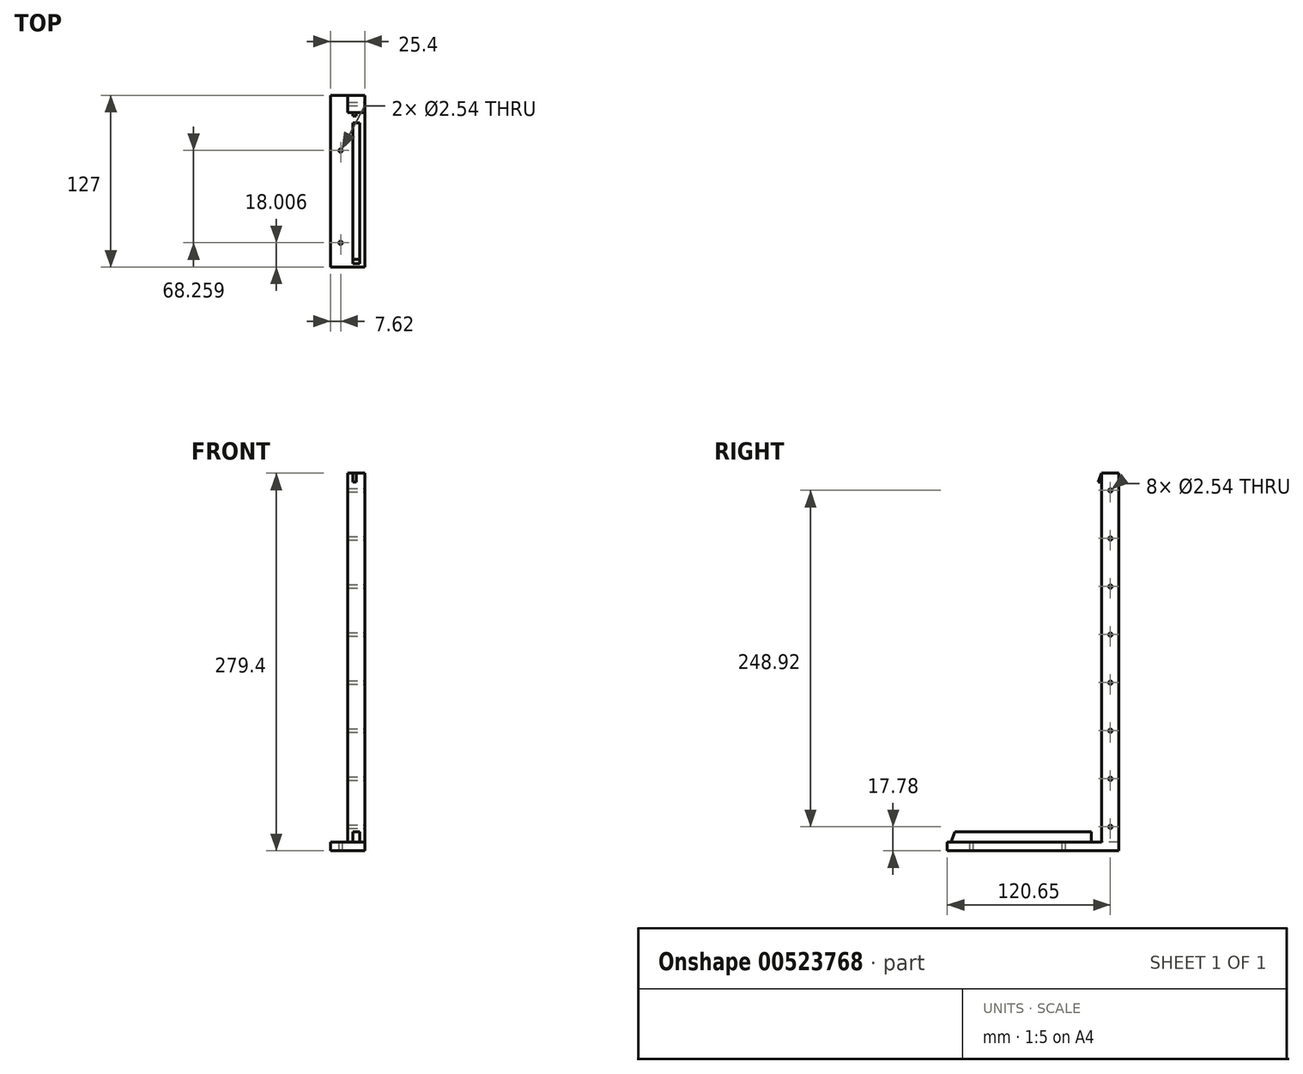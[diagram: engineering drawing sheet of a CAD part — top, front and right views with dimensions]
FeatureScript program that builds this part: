
annotation { "Feature Type Name" : "Feature", "Feature Type Description" : "" }
export const myFeature = defineFeature(function(context is Context, id is Id, definition is map)
    precondition{}
    {
        {
            var Q0;
            Q0=qCreatedBy(makeId("Top.planeOp"),FACE);
            var sketch = newSketch(context, id + "F0", { "sketchPlane" : qUnion([Q0])});
            skLineSegment(sketch, "E0.bottom", {"start": v(0, 0) * mm, "end": v(-25.4, 0) * mm});
            skLineSegment(sketch, "E0.top", {"start": v(0, 127) * mm, "end": v(-25.4, 127) * mm});
            skLineSegment(sketch, "E0.left", {"start": v(0, 0) * mm, "end": v(0, 127) * mm});
            skLineSegment(sketch, "E0.right", {"start": v(-25.4, 0) * mm, "end": v(-25.4, 127) * mm});
            skSolve(sketch);
        }
        {
            var Q0;
            Q0=makeQuery(id+"F0.imprint","IMPRINT",FACE,{"disambiguationData":[TD([[makeQuery(id+"F0.imprint","IMPRINT",EDGE,{"derivedFrom":sQuery(id+"F0.wireOp",EDGE,"E0.bottom")}),-1.0]])]});
            extrude(context, id + "F1", {"entities" : qUnion([Q0]), "depth" : 6.35 * mm, "offsetDistance" : 25.4 * mm});
        }
        {
            var Q0;
            Q0=makeQuery(id+"F1.opExtrude","CAP_FACE",FACE,{"disambiguationData":[OSD([sQuery(id+"F0.wireOp",EDGE,"E0.bottom"),sQuery(id+"F0.wireOp",EDGE,"E0.top"),sQuery(id+"F0.wireOp",EDGE,"E0.left"),sQuery(id+"F0.wireOp",EDGE,"E0.right")])],"isStart":false});
            var sketch = newSketch(context, id + "F2", { "sketchPlane" : qUnion([Q0])});
            skLineSegment(sketch, "E1.bottom", {"start": v(-25.4, 127) * mm, "end": v(-12.7, 127) * mm});
            skLineSegment(sketch, "E1.top", {"start": v(-25.4, 114.3) * mm, "end": v(-12.7, 114.3) * mm});
            skLineSegment(sketch, "E1.left", {"start": v(-25.4, 127) * mm, "end": v(-25.4, 114.3) * mm});
            skLineSegment(sketch, "E1.right", {"start": v(-12.7, 127) * mm, "end": v(-12.7, 114.3) * mm});
            skSolve(sketch);
        }
        {
            var Q0;
            Q0=makeQuery(id+"F2.imprint","IMPRINT",FACE,{"disambiguationData":[TD([[makeQuery(id+"F2.imprint","IMPRINT",EDGE,{"derivedFrom":sQuery(id+"F2.wireOp",EDGE,"E1.bottom")}),1.0]])]});
            extrude(context, id + "F3", {"entities" : qUnion([Q0]), "operationType" : NewBodyOperationType.ADD, "depth" : 273.05 * mm, "offsetDistance" : 25.4 * mm});
        }
        {
            var Q0;
            Q0=makeQuery(id+"F3.opExtrude","SWEPT_FACE",FACE,{"disambiguationData":[OSD([sQuery(id+"F2.wireOp",EDGE,"E1.top")])]});
            var sketch = newSketch(context, id + "F4", { "sketchPlane" : qUnion([Q0])});
            skLineSegment(sketch, "E2", {"start": v(-19.05, 279.4) * mm, "end": v(-19.05, 272.87) * mm});
            skLineSegment(sketch, "E3", {"start": v(-19.05, 272.87) * mm, "end": v(-21.59, 272.87) * mm});
            skLineSegment(sketch, "E4.top", {"start": v(-19.05, 279.4) * mm, "end": v(-21.59, 279.4) * mm});
            skLineSegment(sketch, "E4.left", {"start": v(-19.05, 272.87) * mm, "end": v(-19.05, 279.4) * mm});
            skLineSegment(sketch, "E4.right", {"start": v(-21.59, 272.87) * mm, "end": v(-21.59, 279.4) * mm});
            skSolve(sketch);
        }
        {
            var Q0;
            Q0=makeQuery(id+"F4.imprint","IMPRINT",FACE,{"disambiguationData":[TD([[makeQuery(id+"F4.imprint","IMPRINT",EDGE,{"derivedFrom":sQuery(id+"F4.wireOp",EDGE,"E3")}),-1.0]])]});
            extrude(context, id + "F5", {"entities" : qUnion([Q0]), "operationType" : NewBodyOperationType.ADD, "depth" : 25.4 * mm, "offsetDistance" : 25.4 * mm});
        }
        {
            var Q0;
            Q0=makeQuery(id+"F5.opExtrude","SWEPT_FACE",FACE,{"disambiguationData":[OSD([sQuery(id+"F4.wireOp",EDGE,"E4.right")])]});
            var sketch = newSketch(context, id + "F6", { "sketchPlane" : qUnion([Q0])});
            skLineSegment(sketch, "E5", {"start": v(-114.3, 279.4) * mm, "end": v(0, 0) * mm});
            skLineSegment(sketch, "E6", {"start": v(0, 0) * mm, "end": v(-114.3, 0) * mm});
            skLineSegment(sketch, "E7", {"start": v(-114.3, 0) * mm, "end": v(-114.3, 279.4) * mm});
            skLineSegment(sketch, "E8", {"start": v(-114.3, 0) * mm, "end": v(-96.32, 0) * mm});
            skLineSegment(sketch, "E9", {"start": v(-114.3, 0) * mm, "end": v(-114.3, 6.35) * mm});
            skLineSegment(sketch, "E10", {"start": v(-114.3, 6.35) * mm, "end": v(-106.68, 6.35) * mm});
            skLineSegment(sketch, "E11", {"start": v(-106.68, 6.35) * mm, "end": v(-106.68, 13.97) * mm});
            skLineSegment(sketch, "E12", {"start": v(-106.68, 13.97) * mm, "end": v(-5.71, 13.97) * mm});
            skLineSegment(sketch, "E13", {"start": v(-5.71, 13.97) * mm, "end": v(-13.34, 13.97) * mm});
            skLineSegment(sketch, "E14", {"start": v(-114.3, 279.4) * mm, "end": v(-114.3, 263.18) * mm});
            skLineSegment(sketch, "E15", {"start": v(-106.68, 13.97) * mm, "end": v(-106.68, 217.25) * mm});
            skLineSegment(sketch, "E16", {"start": v(-106.68, 217.25) * mm, "end": v(-106.68, 237.58) * mm});
            skLineSegment(sketch, "E17", {"start": v(-106.68, 237.58) * mm, "end": v(-13.33, 13.97) * mm});
            skSolve(sketch);
        }
        {
            var Q0;
            {var subQ5=sQuery(id+"F6.wireOp",EDGE,"E7");Q0=makeQuery(id+"F6.imprint","IMPRINT",FACE,{"disambiguationData":[TD([[makeQuery(id+"F6.imprint","IMPRINT",EDGE,{"derivedFrom":subQ5}),-1.0]])]});}
            var Q1;
            {var subQ0=sQuery(id+"F6.wireOp",EDGE,"E6");Q1=makeQuery(id+"F6.imprint","IMPRINT",FACE,{"disambiguationData":[TD([[makeQuery(id+"F6.imprint","IMPRINT",EDGE,{"derivedFrom":subQ0}),-1.0]])]});}
            extrude(context, id + "F7", {"entities" : qUnion([Q0, Q1]), "operationType" : NewBodyOperationType.ADD, "oppositeDirection" : true, "depth" : 5.08 * mm, "offsetDistance" : 25.4 * mm});
        }
        {
            var Q0;
            Q0=makeQuery(id+"F5.opExtrude","CAP_FACE",FACE,{"disambiguationData":[OSD([sQuery(id+"F4.wireOp",EDGE,"E3"),sQuery(id+"F4.wireOp",EDGE,"E4.top"),sQuery(id+"F4.wireOp",EDGE,"E4.left"),sQuery(id+"F4.wireOp",EDGE,"E4.right")])],"isStart":false});
            extrude(context, id + "F8", {"entities" : qUnion([Q0]), "operationType" : NewBodyOperationType.REMOVE, "oppositeDirection" : true, "depth" : 25.4 * mm, "offsetDistance" : 25.4 * mm});
        }
        {
            var Q0;
            Q0=makeQuery(id+"F1.opExtrude","CAP_FACE",FACE,{"disambiguationData":[OSD([sQuery(id+"F0.wireOp",EDGE,"E0.bottom"),sQuery(id+"F0.wireOp",EDGE,"E0.top"),sQuery(id+"F0.wireOp",EDGE,"E0.left"),sQuery(id+"F0.wireOp",EDGE,"E0.right")])],"isStart":false});
            var sketch = newSketch(context, id + "F9", { "sketchPlane" : qUnion([Q0])});
            skLineSegment(sketch, "E18", {"start": v(0, 18) * mm, "end": v(-7.62, 18) * mm});
            skLineSegment(sketch, "E19", {"start": v(-7.62, 18) * mm, "end": v(-7.62, 86.27) * mm});
            skCircle(sketch, "E20", {"center": v(-7.62, 86.27) * mm, "radius": 1.27 * mm});
            skCircle(sketch, "E21", {"center": v(-7.62, 18) * mm, "radius": 1.27 * mm});
            skSolve(sketch);
        }
        {
            var Q0;
            Q0=makeQuery(id+"F9.imprint","IMPRINT",FACE,{"disambiguationData":[TD([[makeQuery(id+"F9.imprint","IMPRINT",EDGE,{"derivedFrom":sQuery(id+"F9.wireOp",EDGE,"E20")}),1.0]])]});
            var Q1;
            {var subQ0=sQuery(id+"F9.wireOp",EDGE,"E19");var subQ1=sQuery(id+"F9.wireOp",EDGE,"E18");var subQ2=makeQuery(id+"F9.imprint","INTERSECT",VERTEX,{"derivedFrom":[subQ1,subQ0]});Q1=makeQuery(id+"F9.imprint","IMPRINT",FACE,{"disambiguationData":[TD([[makeQuery(id+"F9.imprint","IMPRINT",EDGE,{"disambiguationData":[TD([[subQ2,1.0]])],"derivedFrom":subQ1}),1.0]])]});}
            var Q2;
            {var subQ0=sQuery(id+"F9.wireOp",EDGE,"E19");var subQ1=sQuery(id+"F9.wireOp",EDGE,"E18");var subQ2=makeQuery(id+"F9.imprint","INTERSECT",VERTEX,{"derivedFrom":[subQ1,subQ0]});Q2=makeQuery(id+"F9.imprint","IMPRINT",FACE,{"disambiguationData":[TD([[makeQuery(id+"F9.imprint","IMPRINT",EDGE,{"disambiguationData":[TD([[subQ2,1.0]])],"derivedFrom":subQ1}),-1.0]])]});}
            extrude(context, id + "F10", {"entities" : qUnion([Q0, Q1, Q2]), "operationType" : NewBodyOperationType.REMOVE, "oppositeDirection" : true, "depth" : 25.4 * mm, "offsetDistance" : 25.4 * mm});
        }
        {
            var Q0;
            Q0=makeQuery(id+"F3.opExtrude","SWEPT_FACE",FACE,{"disambiguationData":[OSD([sQuery(id+"F2.wireOp",EDGE,"E1.right")])]});
            var sketch = newSketch(context, id + "F11", { "sketchPlane" : qUnion([Q0])});
            skLineSegment(sketch, "E22", {"start": v(120.65, 279.4) * mm, "end": v(120.65, 266.7) * mm});
            skCircle(sketch, "E23", {"center": v(120.65, 266.7) * mm, "radius": 1.27 * mm});
            skCircle(sketch, "E24.0.1.0", {"center": v(120.65, 231.14) * mm, "radius": 1.27 * mm});
            skCircle(sketch, "E24.0.2.0", {"center": v(120.65, 195.58) * mm, "radius": 1.27 * mm});
            skCircle(sketch, "E24.0.3.0", {"center": v(120.65, 160.02) * mm, "radius": 1.27 * mm});
            skCircle(sketch, "E24.0.4.0", {"center": v(120.65, 124.46) * mm, "radius": 1.27 * mm});
            skCircle(sketch, "E24.0.5.0", {"center": v(120.65, 88.9) * mm, "radius": 1.27 * mm});
            skCircle(sketch, "E24.0.6.0", {"center": v(120.65, 53.34) * mm, "radius": 1.27 * mm});
            skCircle(sketch, "E24.0.7.0", {"center": v(120.65, 17.78) * mm, "radius": 1.27 * mm});
            skLineSegment(sketch, "E24.direction1", {"start": v(120.65, 266.7) * mm, "end": v(146.05, 266.7) * mm, "construction": true});
            skLineSegment(sketch, "E24.direction2", {"start": v(120.65, 266.7) * mm, "end": v(120.65, 231.14) * mm, "construction": true});
            skSolve(sketch);
        }
        {
            var Q0;
            Q0=makeQuery(id+"F11.imprint","IMPRINT",FACE,{"disambiguationData":[TD([[makeQuery(id+"F11.imprint","IMPRINT",EDGE,{"derivedFrom":sQuery(id+"F11.wireOp",EDGE,"E23")}),1.0]])]});
            var Q1;
            Q1=makeQuery(id+"F11.imprint","IMPRINT",FACE,{"disambiguationData":[TD([[makeQuery(id+"F11.imprint","IMPRINT",EDGE,{"derivedFrom":sQuery(id+"F11.wireOp",EDGE,"E24.0.1.0")}),1.0]])]});
            var Q2;
            Q2=makeQuery(id+"F11.imprint","IMPRINT",FACE,{"disambiguationData":[TD([[makeQuery(id+"F11.imprint","IMPRINT",EDGE,{"derivedFrom":sQuery(id+"F11.wireOp",EDGE,"E24.0.2.0")}),1.0]])]});
            var Q3;
            Q3=makeQuery(id+"F11.imprint","IMPRINT",FACE,{"disambiguationData":[TD([[makeQuery(id+"F11.imprint","IMPRINT",EDGE,{"derivedFrom":sQuery(id+"F11.wireOp",EDGE,"E24.0.3.0")}),1.0]])]});
            var Q4;
            Q4=makeQuery(id+"F11.imprint","IMPRINT",FACE,{"disambiguationData":[TD([[makeQuery(id+"F11.imprint","IMPRINT",EDGE,{"derivedFrom":sQuery(id+"F11.wireOp",EDGE,"E24.0.4.0")}),1.0]])]});
            var Q5;
            Q5=makeQuery(id+"F11.imprint","IMPRINT",FACE,{"disambiguationData":[TD([[makeQuery(id+"F11.imprint","IMPRINT",EDGE,{"derivedFrom":sQuery(id+"F11.wireOp",EDGE,"E24.0.5.0")}),1.0]])]});
            var Q6;
            Q6=makeQuery(id+"F11.imprint","IMPRINT",FACE,{"disambiguationData":[TD([[makeQuery(id+"F11.imprint","IMPRINT",EDGE,{"derivedFrom":sQuery(id+"F11.wireOp",EDGE,"E24.0.6.0")}),1.0]])]});
            var Q7;
            Q7=makeQuery(id+"F11.imprint","IMPRINT",FACE,{"disambiguationData":[TD([[makeQuery(id+"F11.imprint","IMPRINT",EDGE,{"derivedFrom":sQuery(id+"F11.wireOp",EDGE,"E24.0.7.0")}),1.0]])]});
            extrude(context, id + "F12", {"entities" : qUnion([Q0, Q1, Q2, Q3, Q4, Q5, Q6, Q7]), "operationType" : NewBodyOperationType.REMOVE, "oppositeDirection" : true, "depth" : 25.4 * mm, "offsetDistance" : 25.4 * mm});
        }
        {
            var Q0;
            Q0=makeQuery(id+"F1.opExtrude","SWEPT_BODY",BODY,{"disambiguationData":[OSD([sQuery(id+"F0.wireOp",EDGE,"E0.bottom"),sQuery(id+"F0.wireOp",EDGE,"E0.top"),sQuery(id+"F0.wireOp",EDGE,"E0.left"),sQuery(id+"F0.wireOp",EDGE,"E0.right")])]});
            var Q1;
            Q1=makeQuery(id+"F3.boolean.opBoolean","MERGE",FACE,{"derivedFrom":[makeQuery(id+"F1.opExtrude","SWEPT_FACE",FACE,{"disambiguationData":[OSD([sQuery(id+"F0.wireOp",EDGE,"E0.right")])]}),makeQuery(id+"F3.opExtrude","SWEPT_FACE",FACE,{"disambiguationData":[OSD([sQuery(id+"F2.wireOp",EDGE,"E1.left")])]})]});
            mirror(context, id + "F13", {"operationType" : NewBodyOperationType.ADD, "entities" : qUnion([Q0]), "mirrorPlane" : qUnion([Q1])});
        }
        {
            var Q0;
            Q0=makeQuery(id+"F1.opExtrude","SWEPT_FACE",FACE,{"disambiguationData":[OSD([sQuery(id+"F0.wireOp",EDGE,"E0.left")])]});
            var sketch = newSketch(context, id + "F14", { "sketchPlane" : qUnion([Q0])});
            skLineSegment(sketch, "E25.bottom", {"start": v(127, 0) * mm, "end": v(-6.41, 0) * mm});
            skLineSegment(sketch, "E25.top", {"start": v(127, 291.75) * mm, "end": v(-6.41, 291.75) * mm});
            skLineSegment(sketch, "E25.left", {"start": v(127, 0) * mm, "end": v(127, 291.75) * mm});
            skLineSegment(sketch, "E25.right", {"start": v(-6.41, 0) * mm, "end": v(-6.41, 291.75) * mm});
            skSolve(sketch);
        }
        {
            var Q0;
            {var subQ4=sQuery(id+"F14.wireOp",EDGE,"E25.top");Q0=makeQuery(id+"F14.imprint","IMPRINT",FACE,{"disambiguationData":[TD([[makeQuery(id+"F14.imprint","IMPRINT",EDGE,{"derivedFrom":subQ4}),1.0]])]});}
            extrude(context, id + "F15", {"entities" : qUnion([Q0]), "operationType" : NewBodyOperationType.REMOVE, "oppositeDirection" : true, "depth" : 25.4 * mm, "offsetDistance" : 25.4 * mm});
        }
        {
            var Q0;
            Q0=makeQuery(id+"F1.opExtrude","SWEPT_FACE",FACE,{"disambiguationData":[OSD([sQuery(id+"F0.wireOp",EDGE,"E0.left")])]});
            var sketch = newSketch(context, id + "F16", { "sketchPlane" : qUnion([Q0])});
            skLineSegment(sketch, "E26.bottom", {"start": v(127, 0) * mm, "end": v(0, 0) * mm});
            skLineSegment(sketch, "E26.top", {"start": v(127, 6.35) * mm, "end": v(0, 6.35) * mm});
            skLineSegment(sketch, "E26.left", {"start": v(127, 0) * mm, "end": v(127, 6.35) * mm});
            skLineSegment(sketch, "E26.right", {"start": v(0, 0) * mm, "end": v(0, 6.35) * mm});
            skSolve(sketch);
        }
        {
            var Q0;
            Q0=makeQuery(id+"F16.imprint","IMPRINT",FACE,{"disambiguationData":[TD([[makeQuery(id+"F16.imprint","IMPRINT",EDGE,{"derivedFrom":sQuery(id+"F16.wireOp",EDGE,"E26.bottom")}),1.0]])]});
            extrude(context, id + "F17", {"entities" : qUnion([Q0]), "operationType" : NewBodyOperationType.REMOVE, "oppositeDirection" : true, "depth" : 25.4 * mm, "offsetDistance" : 25.4 * mm});
        }
    });
